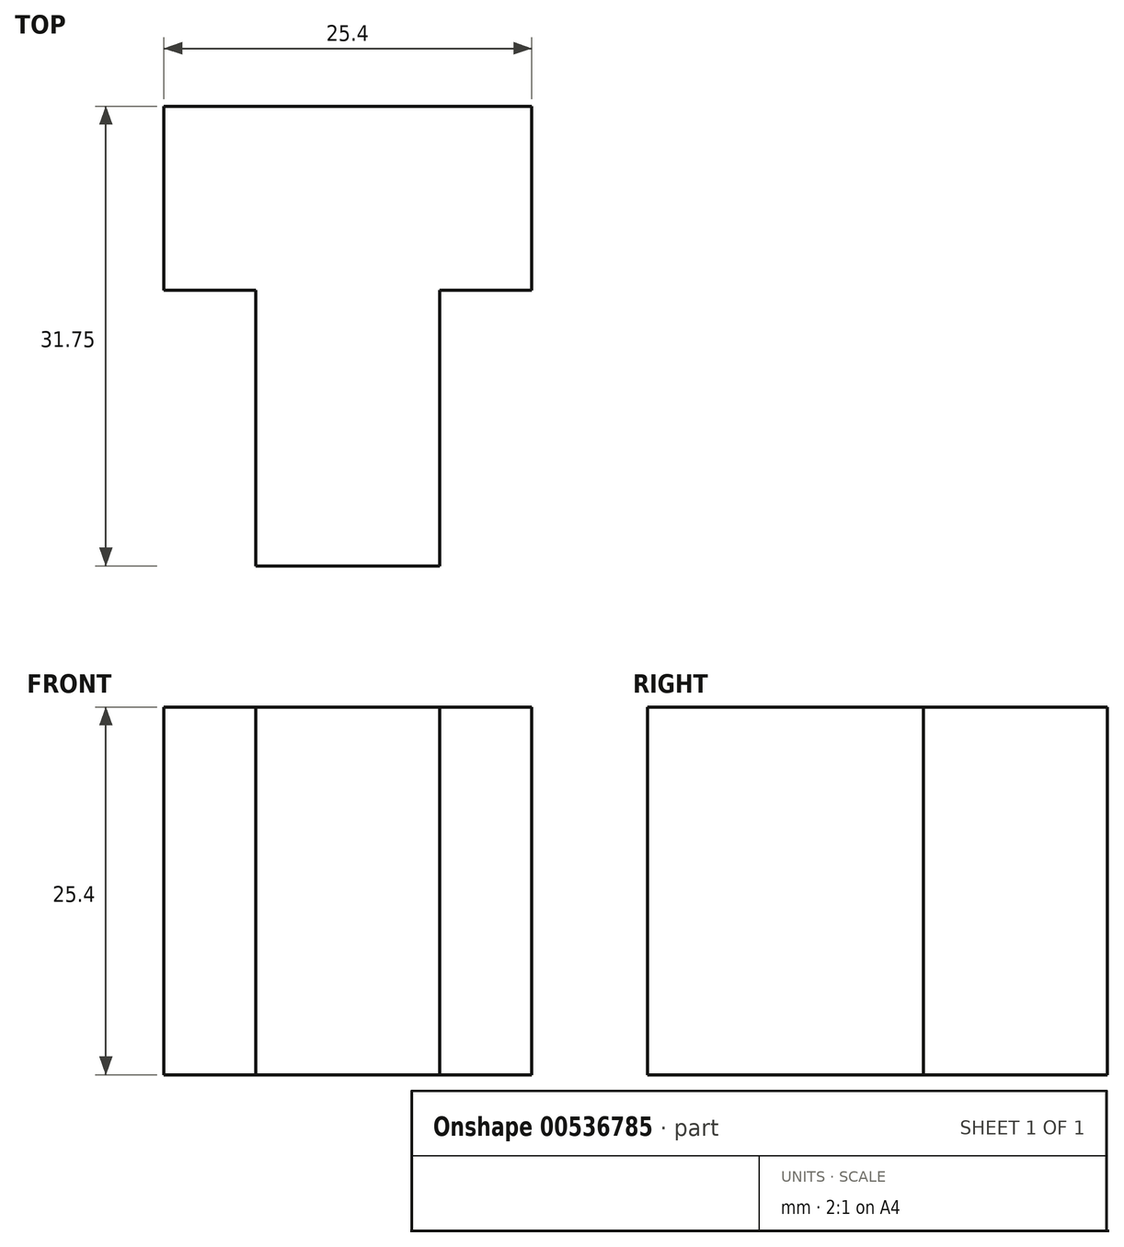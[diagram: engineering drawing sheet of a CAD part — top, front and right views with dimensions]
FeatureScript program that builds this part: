
annotation { "Feature Type Name" : "Feature", "Feature Type Description" : "" }
export const myFeature = defineFeature(function(context is Context, id is Id, definition is map)
    precondition{}
    {
        {
            var Q0;
            Q0=qCreatedBy(makeId("Top.planeOp"),FACE);
            var sketch = newSketch(context, id + "F0", { "sketchPlane" : qUnion([Q0])});
            skLineSegment(sketch, "E0", {"start": v(0, 0) * mm, "end": v(0, 31.75) * mm});
            skLineSegment(sketch, "E1", {"start": v(0, 31.75) * mm, "end": v(25.4, 31.75) * mm});
            skLineSegment(sketch, "E2", {"start": v(25.4, 31.75) * mm, "end": v(25.4, 19.05) * mm});
            skLineSegment(sketch, "E3", {"start": v(25.4, 19.05) * mm, "end": v(19.05, 19.05) * mm});
            skLineSegment(sketch, "E4", {"start": v(19.05, 19.05) * mm, "end": v(19.05, 0) * mm});
            skLineSegment(sketch, "E5", {"start": v(19.05, 0) * mm, "end": v(6.35, 0) * mm});
            skLineSegment(sketch, "E6", {"start": v(6.35, 0) * mm, "end": v(6.35, 19.05) * mm});
            skLineSegment(sketch, "E7", {"start": v(6.35, 19.05) * mm, "end": v(0, 19.05) * mm});
            skSolve(sketch);
        }
        {
            var Q0;
            Q0 = qSketchRegion(id + "F0", true);
            extrude(context, id + "F1", {"entities" : qUnion([Q0]), "depth" : 25.4 * mm, "offsetDistance" : 25.4 * mm});
        }
    });
